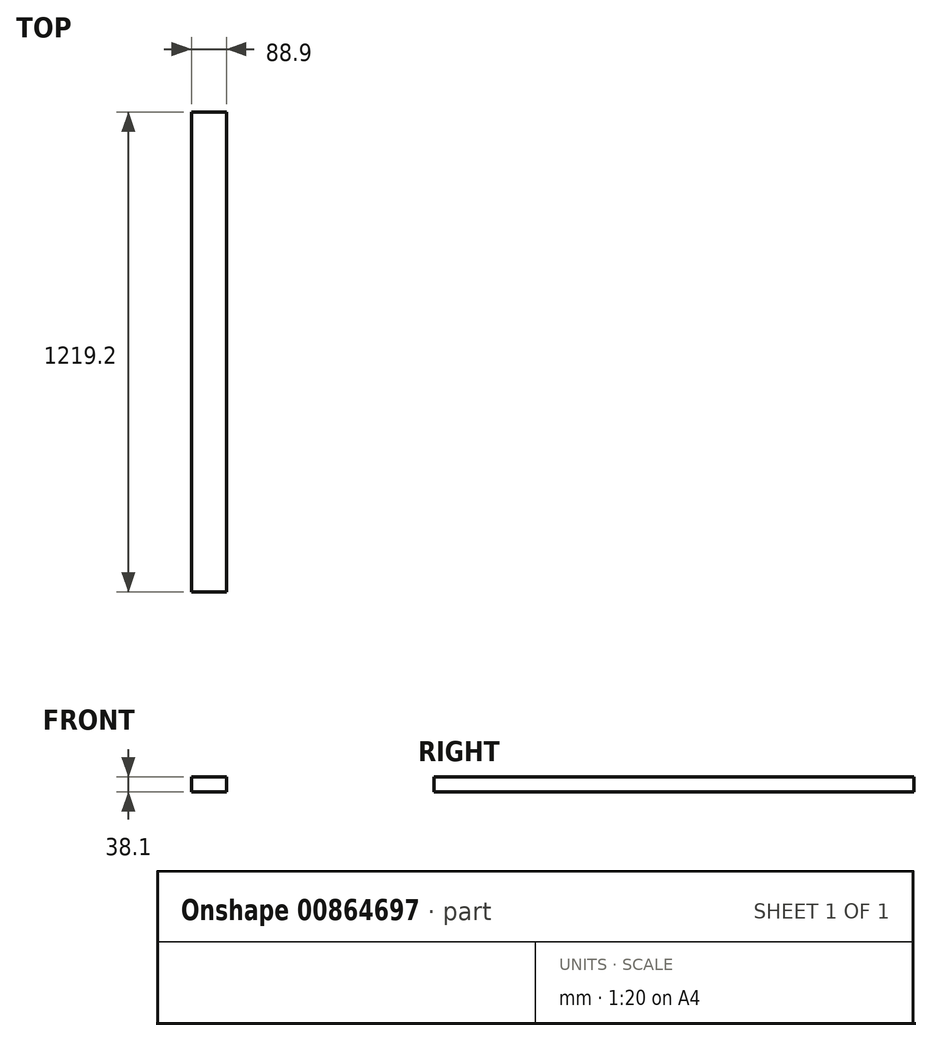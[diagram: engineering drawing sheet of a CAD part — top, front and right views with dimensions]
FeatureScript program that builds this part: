
annotation { "Feature Type Name" : "Feature", "Feature Type Description" : "" }
export const myFeature = defineFeature(function(context is Context, id is Id, definition is map)
    precondition{}
    {
        {
            var Q0;
            Q0=qCreatedBy(makeId("Front.planeOp"),FACE);
            var sketch = newSketch(context, id + "F0", { "sketchPlane" : qUnion([Q0])});
            skLineSegment(sketch, "E0.bottom", {"start": v(0, 0) * mm, "end": v(88.9, 0) * mm});
            skLineSegment(sketch, "E0.top", {"start": v(0, 38.1) * mm, "end": v(88.9, 38.1) * mm});
            skLineSegment(sketch, "E0.left", {"start": v(0, 0) * mm, "end": v(0, 38.1) * mm});
            skLineSegment(sketch, "E0.right", {"start": v(88.9, 0) * mm, "end": v(88.9, 38.1) * mm});
            skSolve(sketch);
        }
        {
            var Q0;
            Q0 = qSketchRegion(id + "F0", true);
            extrude(context, id + "F1", {"entities" : qUnion([Q0]), "oppositeDirection" : true, "depth" : 1219.2 * mm, "offsetDistance" : 25.4 * mm});
        }
    });
